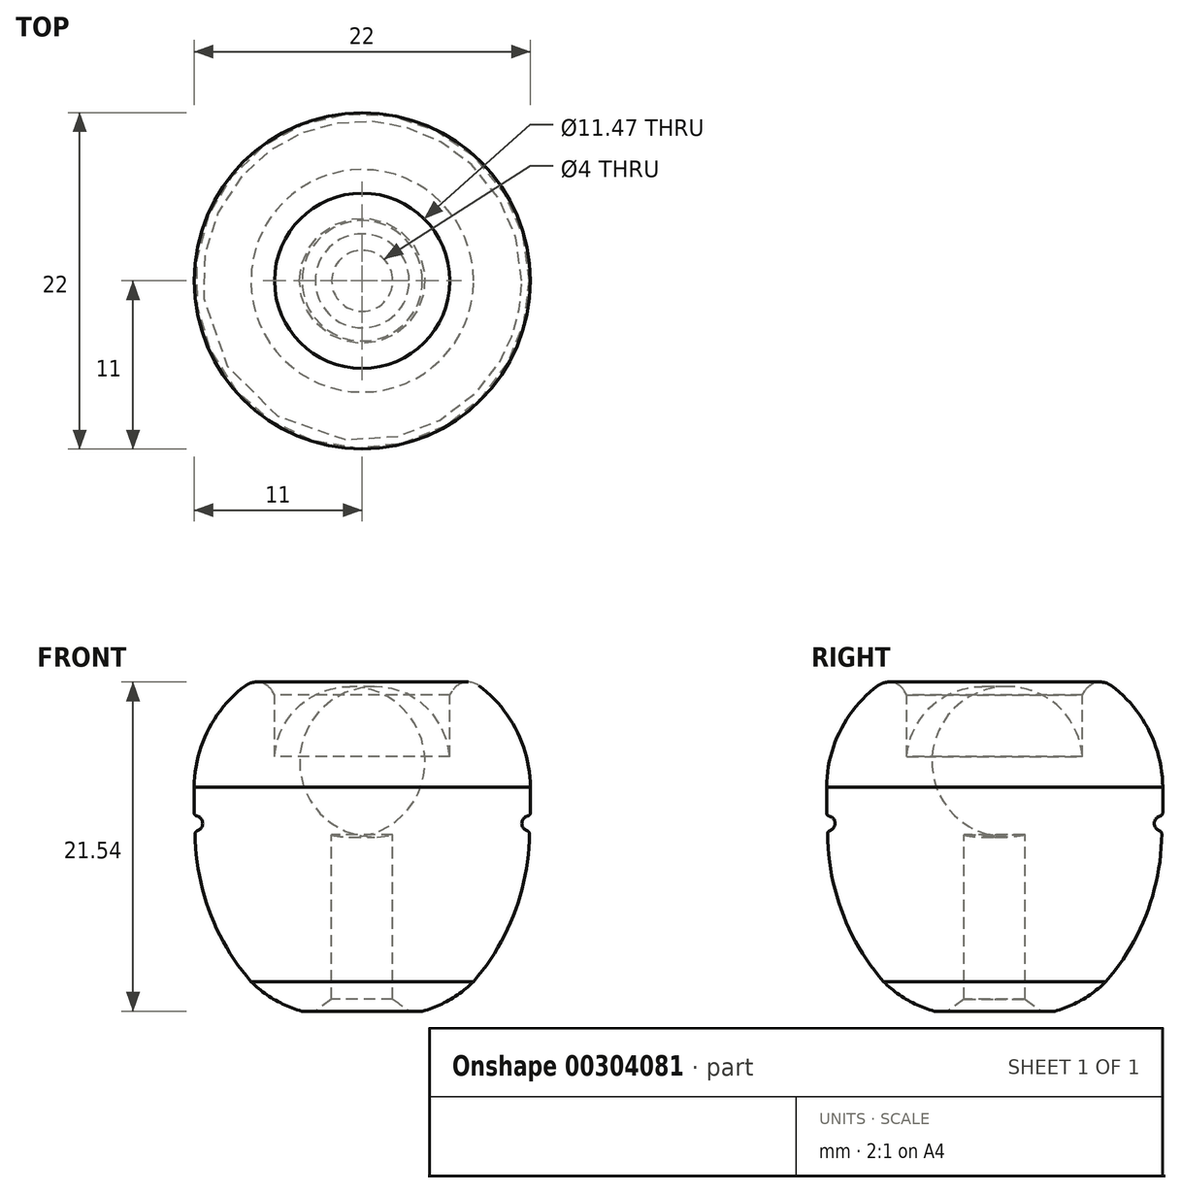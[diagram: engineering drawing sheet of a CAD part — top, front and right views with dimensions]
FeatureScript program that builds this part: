
annotation { "Feature Type Name" : "Feature", "Feature Type Description" : "" }
export const myFeature = defineFeature(function(context is Context, id is Id, definition is map)
    precondition{}
    {
        {
            var Q0;
            Q0=qCreatedBy(makeId("Front.planeOp"),FACE);
            var sketch = newSketch(context, id + "F0", { "sketchPlane" : qUnion([Q0])});
            skPoint(sketch, "E0.endSnap0", {"position": v(3.5, 4.5) * mm});
            skLineSegment(sketch, "E1", {"start": v(2, 0.79) * mm, "end": v(3.07, 0) * mm});
            skPoint(sketch, "E2.startSnap0", {"position": v(11, 11) * mm});
            skArc(sketch, "E3", {"start": v(2, 11.53) * mm, "mid": v(4.8, 13.4) * mm, "end": v(5.74, 16.64) * mm});
            skLineSegment(sketch, "E4", {"start": v(2, 11.53) * mm, "end": v(2, 0.79) * mm});
            skLineSegment(sketch, "E5", {"start": v(5.74, 16.64) * mm, "end": v(5.74, 20.68) * mm});
            skLineSegment(sketch, "E6", {"start": v(5.74, 20.68) * mm, "end": v(5.9, 20.96) * mm});
            skArc(sketch, "E7", {"start": v(11, 14.67) * mm, "mid": v(10.1, 18.37) * mm, "end": v(7.64, 21.3) * mm});
            skPoint(sketch, "E8.visualSharp", {"position": v(6.53, 22) * mm});
            skArc(sketch, "E8.filletArc", {"start": v(7.64, 21.3) * mm, "mid": v(6.7, 21.51) * mm, "end": v(5.9, 20.96) * mm});
            skLineSegment(sketch, "E9", {"start": v(11, 14.67) * mm, "end": v(11, 12.97) * mm});
            skLineSegment(sketch, "E10", {"start": v(3.94, 0) * mm, "end": v(3.07, 0) * mm});
            skLineSegment(sketch, "E11", {"start": v(0, 12.28) * mm, "end": v(0, 4.07) * mm});
            skArc(sketch, "E12", {"start": v(10.84, 12.77) * mm, "mid": v(10.44, 12.3) * mm, "end": v(10.8, 11.8) * mm});
            skArc(sketch, "E13", {"start": v(7.28, 1.94) * mm, "mid": v(9.97, 6.45) * mm, "end": v(10.94, 11.61) * mm});
            skPoint(sketch, "E14.visualSharp", {"position": v(11, 12.78) * mm});
            skArc(sketch, "E14.filletArc", {"start": v(10.84, 12.77) * mm, "mid": v(10.96, 12.84) * mm, "end": v(11, 12.97) * mm});
            skPoint(sketch, "E15.visualSharp", {"position": v(10.94, 11.78) * mm});
            skArc(sketch, "E15.filletArc", {"start": v(10.94, 11.61) * mm, "mid": v(10.9, 11.73) * mm, "end": v(10.8, 11.8) * mm});
            skPoint(sketch, "E16.visualSharp", {"position": v(5.25, 0) * mm});
            skArc(sketch, "E17", {"start": v(3.94, 0) * mm, "mid": v(5.74, 0.75) * mm, "end": v(7.28, 1.94) * mm});
            skPoint(sketch, "E18.orphan", {"position": v(4.8, 0) * mm});
            skSolve(sketch);
        }
        {
            var Q0;
            Q0=makeQuery(id+"F0.imprint","IMPRINT",FACE,{"disambiguationData":[TD([[makeQuery(id+"F0.imprint","IMPRINT",EDGE,{"derivedFrom":sQuery(id+"F0.wireOp",EDGE,"E1")}),1.0]])]});
            var Q1;
            Q1=sQuery(id+"F0.wireOp",EDGE,"E11");
            revolve(context, id + "F1", {"entities" : qUnion([Q0]), "axis" : qUnion([Q1]), "revolveType" : RevolveType.FULL});
        }
    });
